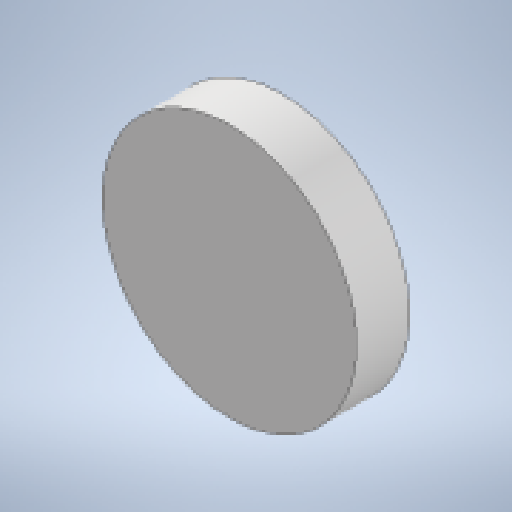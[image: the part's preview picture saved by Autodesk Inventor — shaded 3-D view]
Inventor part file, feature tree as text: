
AUTODESK INVENTOR PART (.ipt)
format: ipt  version: 2023 (Build 270158000, 158)  size: 130,560 bytes
history: native  units: in
note: dims shown in document units (in); Inventor stores cm internally (conversion verified against a paired STEP export)
features: extrude x1, sketch x1
ambient origin geometry x8: Origin, YZ Plane, XZ Plane, XY Plane, X Axis, Y Axis, Z Axis, Center Point
bodies: Solid1 (feature_tree)
feature tree (2):
  extrude  "Extrusion1"  Depth=0.1969in TaperAngle=0.0deg
  sketch  "Sketch1"  dims[d0=0.9449in d1=0.1969in d2=0.0in d3=0.5906in]
